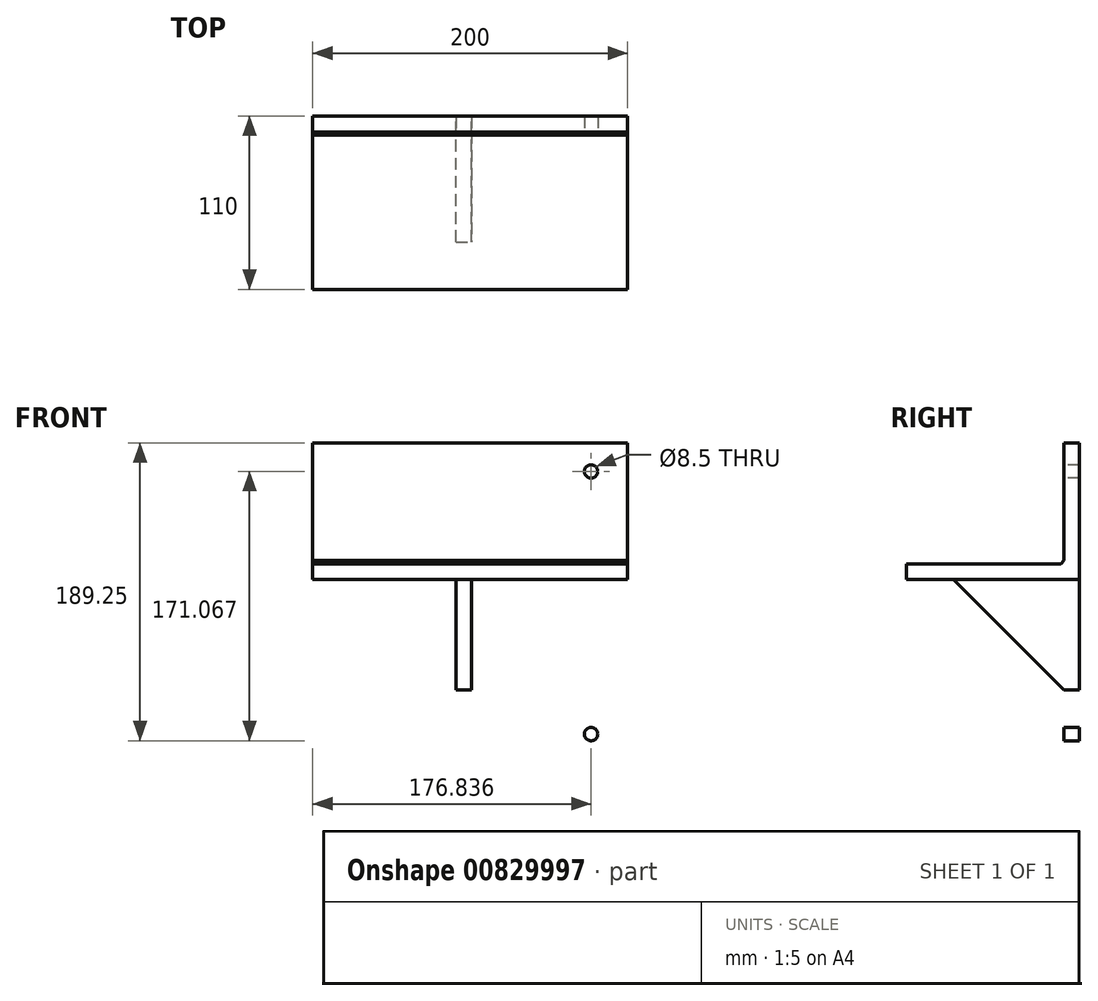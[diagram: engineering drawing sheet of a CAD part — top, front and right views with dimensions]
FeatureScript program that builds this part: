
annotation { "Feature Type Name" : "Feature", "Feature Type Description" : "" }
export const myFeature = defineFeature(function(context is Context, id is Id, definition is map)
    precondition{}
    {
        {
            var Q0;
            Q0=qCreatedBy(makeId("Front.planeOp"),FACE);
            var sketch = newSketch(context, id + "F0", { "sketchPlane" : qUnion([Q0])});
            skLineSegment(sketch, "E0.bottom", {"start": v(-95.92, 101.6) * mm, "end": v(104.08, 101.6) * mm});
            skLineSegment(sketch, "E0.top", {"start": v(-95.92, -98.4) * mm, "end": v(104.08, -98.4) * mm});
            skLineSegment(sketch, "E0.left", {"start": v(-95.92, 101.6) * mm, "end": v(-95.92, -98.4) * mm});
            skLineSegment(sketch, "E0.right", {"start": v(104.08, 101.6) * mm, "end": v(104.08, -98.4) * mm});
            skSolve(sketch);
        }
        {
            var Q0;
            Q0=makeQuery(id+"F0.imprint","IMPRINT",FACE,{"disambiguationData":[TD([[makeQuery(id+"F0.imprint","IMPRINT",EDGE,{"derivedFrom":sQuery(id+"F0.wireOp",EDGE,"E0.bottom")}),-1.0]])]});
            extrude(context, id + "F1", {"entities" : qUnion([Q0]), "depth" : 10 * mm, "offsetDistance" : 25 * mm});
        }
        {
            var Q0;
            Q0=makeQuery(id+"F1.opExtrude","CAP_FACE",FACE,{"disambiguationData":[OSD([sQuery(id+"F0.wireOp",EDGE,"E0.bottom"),sQuery(id+"F0.wireOp",EDGE,"E0.top"),sQuery(id+"F0.wireOp",EDGE,"E0.left"),sQuery(id+"F0.wireOp",EDGE,"E0.right")])],"isStart":false});
            var sketch = newSketch(context, id + "F2", { "sketchPlane" : qUnion([Q0])});
            skLineSegment(sketch, "E1", {"start": v(-95.92, 14.8) * mm, "end": v(104.08, 14.8) * mm});
            skLineSegment(sketch, "E2", {"start": v(-95.92, 24.8) * mm, "end": v(104.08, 24.8) * mm});
            skSolve(sketch);
        }
        {
            var Q0;
            {var subQ0=sQuery(id+"F2.wireOp",EDGE,"E1");Q0=makeQuery(id+"F2.imprint","IMPRINT",FACE,{"disambiguationData":[TD([[makeQuery(id+"F2.imprint","IMPRINT",EDGE,{"derivedFrom":subQ0}),1.0]])]});}
            extrude(context, id + "F3", {"entities" : qUnion([Q0]), "operationType" : NewBodyOperationType.ADD, "depth" : 100 * mm, "offsetDistance" : 25 * mm});
        }
        {
            var Q0;
            {var subQ0=sQuery(id+"F0.wireOp",EDGE,"E0.right");var subQ1=sQuery(id+"F0.wireOp",EDGE,"E0.left");var subQ2=sQuery(id+"F0.wireOp",EDGE,"E0.top");Q0=makeQuery(id+"F3.boolean.opBoolean","SPLIT",FACE,{"disambiguationData":[TD([makeQuery(id+"F1.opExtrude","SWEPT_FACE",FACE,{"disambiguationData":[OSD([subQ2])]})])],"derivedFrom":makeQuery(id+"F1.opExtrude","CAP_FACE",FACE,{"disambiguationData":[OSD([sQuery(id+"F0.wireOp",EDGE,"E0.bottom"),subQ2,subQ1,subQ0])],"isStart":false})});}
            var sketch = newSketch(context, id + "F4", { "sketchPlane" : qUnion([Q0])});
            skLineSegment(sketch, "E3", {"start": v(-5, 14.8) * mm, "end": v(-5, -55.2) * mm});
            skLineSegment(sketch, "E4", {"start": v(-5, -55.2) * mm, "end": v(0, -55.2) * mm});
            skLineSegment(sketch, "E5.MirrorCS", {"start": v(5, 14.8) * mm, "end": v(5, -55.2) * mm});
            skLineSegment(sketch, "E6.MirrorCS", {"start": v(5, -55.2) * mm, "end": v(0, -55.2) * mm});
            skSolve(sketch);
        }
        {
            var Q0;
            {var subQ1=sQuery(id+"F4.wireOp",EDGE,"E3");Q0=makeQuery(id+"F4.imprint","IMPRINT",FACE,{"disambiguationData":[TD([[makeQuery(id+"F4.imprint","IMPRINT",EDGE,{"derivedFrom":subQ1}),1.0]])]});}
            extrude(context, id + "F5", {"entities" : qUnion([Q0]), "operationType" : NewBodyOperationType.ADD, "depth" : 70 * mm, "offsetDistance" : 25 * mm});
        }
        {
            var Q0;
            Q0=makeQuery(id+"F5.opExtrude","SWEPT_FACE",FACE,{"disambiguationData":[OSD([sQuery(id+"F4.wireOp",EDGE,"E3")])]});
            var sketch = newSketch(context, id + "F6", { "sketchPlane" : qUnion([Q0])});
            skLineSegment(sketch, "E7", {"start": v(80, 14.8) * mm, "end": v(10, -55.2) * mm});
            skSolve(sketch);
        }
        {
            var Q0;
            Q0=makeQuery(id+"F6.imprint","IMPRINT",FACE,{"disambiguationData":[TD([[makeQuery(id+"F6.imprint","IMPRINT",EDGE,{"derivedFrom":sQuery(id+"F6.wireOp",EDGE,"E7")}),1.0]])]});
            extrude(context, id + "F7", {"entities" : qUnion([Q0]), "operationType" : NewBodyOperationType.REMOVE, "oppositeDirection" : true, "depth" : 25 * mm, "offsetDistance" : 25 * mm});
        }
        {
            var Q0;
            {var subQ0=sQuery(id+"F0.wireOp",EDGE,"E0.right");var subQ1=sQuery(id+"F0.wireOp",EDGE,"E0.left");var subQ2=sQuery(id+"F0.wireOp",EDGE,"E0.top");Q0=makeQuery(id+"F3.boolean.opBoolean","SPLIT",FACE,{"disambiguationData":[TD([makeQuery(id+"F1.opExtrude","SWEPT_FACE",FACE,{"disambiguationData":[OSD([subQ2])]})])],"derivedFrom":makeQuery(id+"F1.opExtrude","CAP_FACE",FACE,{"disambiguationData":[OSD([sQuery(id+"F0.wireOp",EDGE,"E0.bottom"),subQ2,subQ1,subQ0])],"isStart":false})});}
            var sketch = newSketch(context, id + "F8", { "sketchPlane" : qUnion([Q0])});
            skCircle(sketch, "E8", {"center": v(-80.92, -83.4) * mm, "radius": 4.25 * mm});
            skCircle(sketch, "E9.MirrorC", {"center": v(-80.92, 83.4) * mm, "radius": 4.25 * mm});
            skCircle(sketch, "E10.MirrorC", {"center": v(80.92, -83.4) * mm, "radius": 4.25 * mm});
            skCircle(sketch, "E11.MirrorC", {"center": v(80.92, 83.4) * mm, "radius": 4.25 * mm});
            skSolve(sketch);
        }
        {
            var Q0;
            Q0=makeQuery(id+"F8.imprint","IMPRINT",FACE,{"disambiguationData":[TD([[makeQuery(id+"F8.imprint","IMPRINT",EDGE,{"derivedFrom":sQuery(id+"F8.wireOp",EDGE,"E8")}),1.0]])]});
            var Q1;
            Q1=makeQuery(id+"F8.imprint","IMPRINT",FACE,{"disambiguationData":[TD([[makeQuery(id+"F8.imprint","IMPRINT",EDGE,{"derivedFrom":sQuery(id+"F8.wireOp",EDGE,"E10.MirrorC")}),-1.0]])]});
            var Q2;
            Q2=makeQuery(id+"F8.imprint","IMPRINT",FACE,{"disambiguationData":[TD([[makeQuery(id+"F8.imprint","IMPRINT",EDGE,{"derivedFrom":sQuery(id+"F8.wireOp",EDGE,"E11.MirrorC")}),1.0]])]});
            var Q3;
            Q3=makeQuery(id+"F8.imprint","IMPRINT",FACE,{"disambiguationData":[TD([[makeQuery(id+"F8.imprint","IMPRINT",EDGE,{"derivedFrom":sQuery(id+"F8.wireOp",EDGE,"E9.MirrorC")}),-1.0]])]});
            extrude(context, id + "F9", {"entities" : qUnion([Q0, Q1, Q2, Q3]), "operationType" : NewBodyOperationType.REMOVE, "oppositeDirection" : true, "depth" : 10 * mm, "offsetDistance" : 25 * mm});
        }
        {
            var Q0;
            {var subQ0=sQuery(id+"F0.wireOp",EDGE,"E0.right");var subQ1=sQuery(id+"F2.wireOp",EDGE,"E1");Q0=makeQuery(id+"F5.boolean.opBoolean","SPLIT",EDGE,{"disambiguationData":[TD([makeQuery(id+"F1.opExtrude","SWEPT_FACE",FACE,{"disambiguationData":[OSD([subQ0])]})])],"derivedFrom":makeQuery(id+"F3.opExtrude","CAP_EDGE",EDGE,{"disambiguationData":[OSD([subQ1])],"isStart":true})});}
            var Q1;
            {var subQ0=sQuery(id+"F2.wireOp",EDGE,"E1");var subQ1=sQuery(id+"F0.wireOp",EDGE,"E0.left");Q1=makeQuery(id+"F5.boolean.opBoolean","SPLIT",EDGE,{"disambiguationData":[TD([makeQuery(id+"F1.opExtrude","SWEPT_FACE",FACE,{"disambiguationData":[OSD([subQ1])]})])],"derivedFrom":makeQuery(id+"F3.opExtrude","CAP_EDGE",EDGE,{"disambiguationData":[OSD([subQ0])],"isStart":true})});}
            var Q2;
            Q2=makeQuery(id+"F5.opExtrude","SWEPT_EDGE",EDGE,{"disambiguationData":[OSD([sQuery(id+"F2.wireOp",EDGE,"E1"),sQuery(id+"F4.wireOp",EDGE,"E5.MirrorCS")])]});
            var Q3;
            Q3=makeQuery(id+"F5.opExtrude","CAP_EDGE",EDGE,{"disambiguationData":[OSD([sQuery(id+"F4.wireOp",EDGE,"E5.MirrorCS")])],"isStart":true});
            var Q4;
            Q4=makeQuery(id+"F5.opExtrude","CAP_EDGE",EDGE,{"disambiguationData":[OSD([sQuery(id+"F4.wireOp",EDGE,"E3")])],"isStart":true});
            var Q5;
            Q5=makeQuery(id+"F5.opExtrude","SWEPT_EDGE",EDGE,{"disambiguationData":[OSD([sQuery(id+"F2.wireOp",EDGE,"E1"),sQuery(id+"F4.wireOp",EDGE,"E3")])]});
            var Q6;
            Q6=makeQuery(id+"F3.opExtrude","CAP_EDGE",EDGE,{"disambiguationData":[OSD([sQuery(id+"F2.wireOp",EDGE,"E2")])],"isStart":true});
            chamfer(context, id + "F10", {"entities" : qUnion([Q0, Q1, Q2, Q3, Q4, Q5, Q6]), "width" : 2 * mm, "tangentPropagation" : true});
        }
    });
